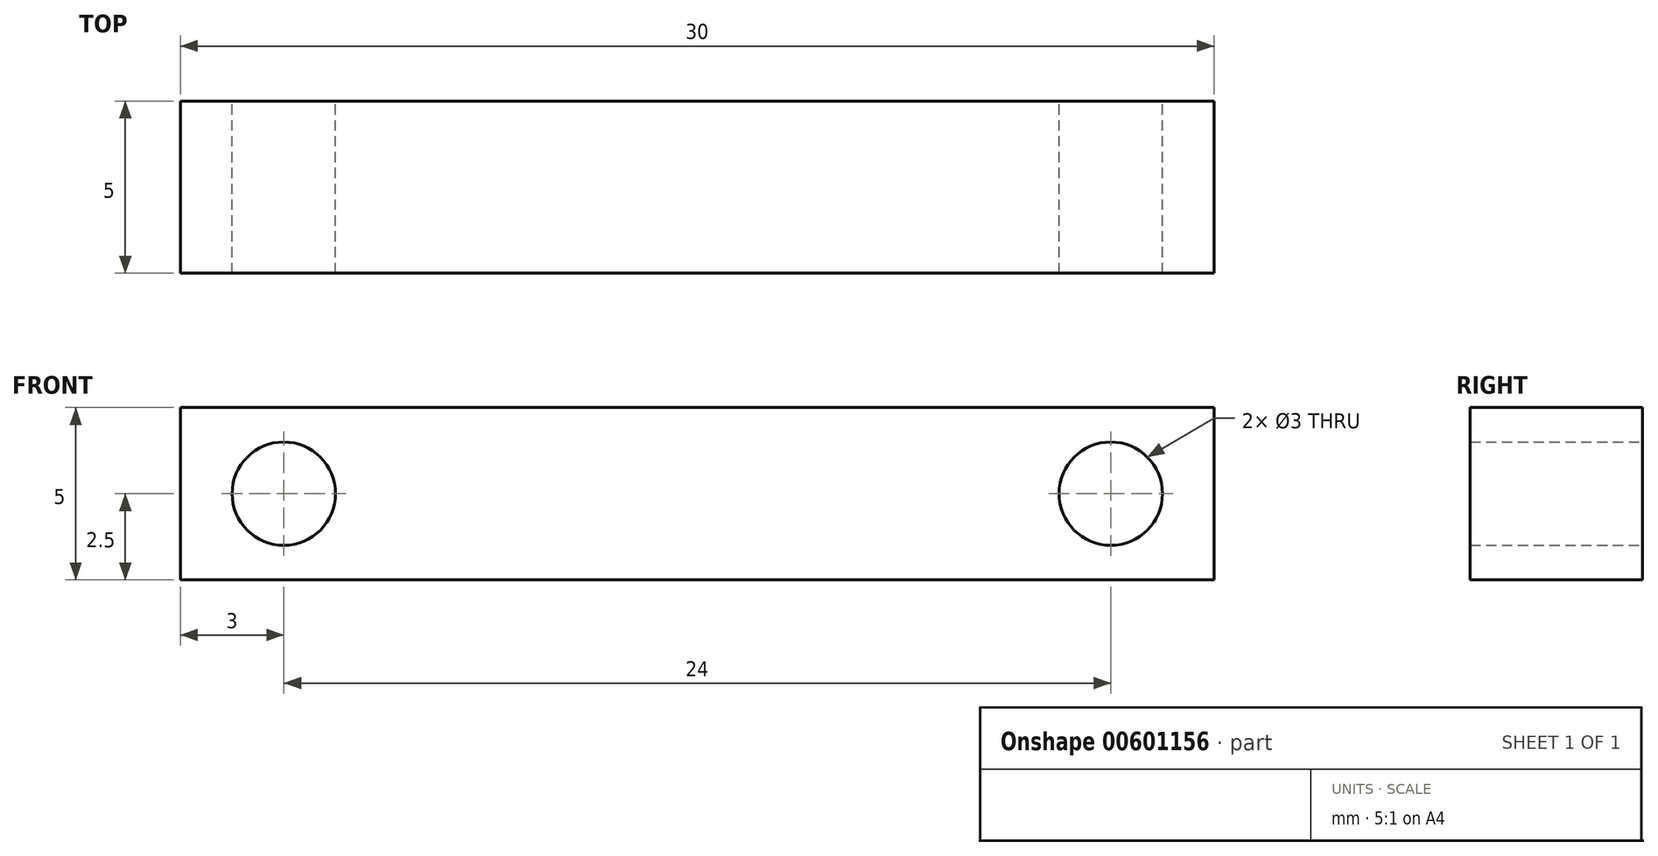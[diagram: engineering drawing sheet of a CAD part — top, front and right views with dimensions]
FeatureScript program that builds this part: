
annotation { "Feature Type Name" : "Feature", "Feature Type Description" : "" }
export const myFeature = defineFeature(function(context is Context, id is Id, definition is map)
    precondition{}
    {
        {
            var Q0;
            Q0=qCreatedBy(makeId("Front.planeOp"),FACE);
            var sketch = newSketch(context, id + "F0", { "sketchPlane" : qUnion([Q0])});
            skLineSegment(sketch, "E0.bottom", {"start": v(0, 0) * mm, "end": v(30, 0) * mm});
            skLineSegment(sketch, "E0.top", {"start": v(0, 5) * mm, "end": v(30, 5) * mm});
            skLineSegment(sketch, "E0.left", {"start": v(0, 0) * mm, "end": v(0, 5) * mm});
            skLineSegment(sketch, "E0.right", {"start": v(30, 0) * mm, "end": v(30, 5) * mm});
            skCircle(sketch, "E1", {"center": v(3, 2.5) * mm, "radius": 1.5 * mm});
            skPoint(sketch, "E1.centerSnap0", {"position": v(0, 2.5) * mm});
            skCircle(sketch, "E2", {"center": v(27, 2.5) * mm, "radius": 1.5 * mm});
            skSolve(sketch);
        }
        {
            var Q0;
            Q0 = qSketchRegion(id + "F0", true);
            extrude(context, id + "F1", {"entities" : qUnion([Q0]), "endBound" : BoundingType.SYMMETRIC, "depth" : 5 * mm, "offsetDistance" : 25.4 * mm});
        }
    });
